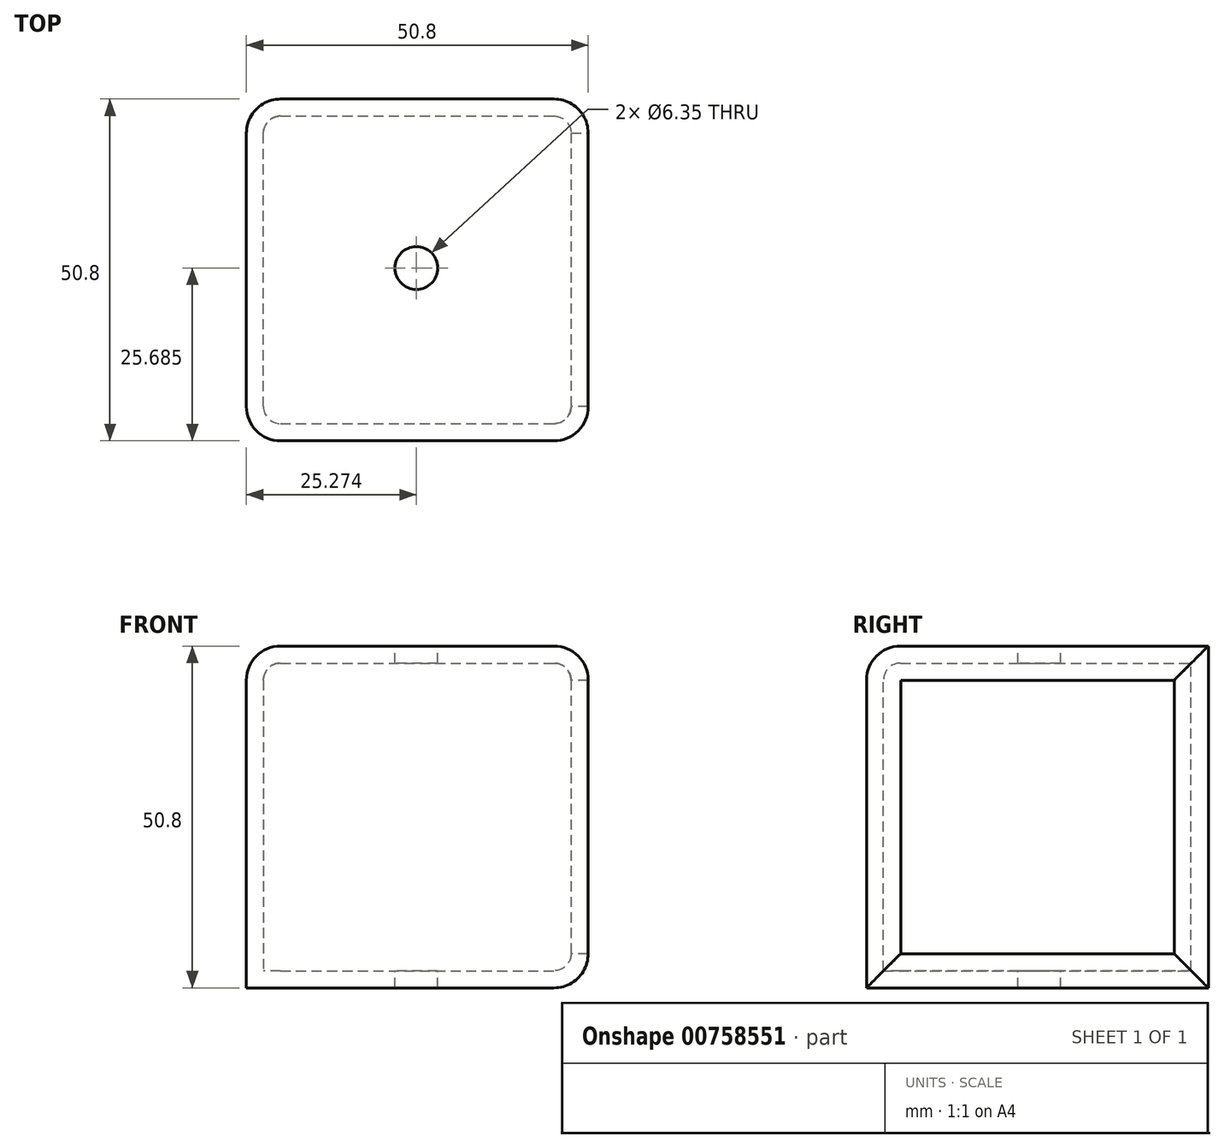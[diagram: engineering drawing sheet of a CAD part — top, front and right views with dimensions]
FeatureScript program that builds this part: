
annotation { "Feature Type Name" : "Feature", "Feature Type Description" : "" }
export const myFeature = defineFeature(function(context is Context, id is Id, definition is map)
    precondition{}
    {
        {
            var Q0;
            Q0=qCreatedBy(makeId("Top.planeOp"),FACE);
            var sketch = newSketch(context, id + "F0", { "sketchPlane" : qUnion([Q0])});
            skLineSegment(sketch, "E0", {"start": v(-54.42, -6.82) * mm, "end": v(-3.62, -6.82) * mm});
            skLineSegment(sketch, "E1", {"start": v(-3.62, -6.82) * mm, "end": v(-54.42, -6.82) * mm});
            skLineSegment(sketch, "E2", {"start": v(-54.42, -6.82) * mm, "end": v(-54.42, -57.62) * mm});
            skLineSegment(sketch, "E3", {"start": v(-54.42, -57.62) * mm, "end": v(-3.62, -57.62) * mm});
            skLineSegment(sketch, "E4", {"start": v(-3.62, -6.82) * mm, "end": v(-3.62, -57.62) * mm});
            skSolve(sketch);
        }
        {
            var Q0;
            Q0=qSketchRegion(id+"F0",true);
            extrude(context, id + "F1", {"entities" : qUnion([Q0]), "depth" : 50.8 * mm, "offsetDistance" : 25.4 * mm});
        }
        {
            var Q0;
            Q0=makeQuery(id+"F1.opExtrude","SWEPT_FACE",FACE,{"disambiguationData":[OSD([sQuery(id+"F0.wireOp",EDGE,"E3")])]});
            var sketch = newSketch(context, id + "F2", { "sketchPlane" : qUnion([Q0])});
            skSolve(sketch);
        }
        {
            var Q0;
            Q0=makeQuery(id+"F1.opExtrude","CAP_EDGE",EDGE,{"disambiguationData":[OSD([sQuery(id+"F0.wireOp",EDGE,"E3")])],"isStart":false});
            var Q1;
            Q1=makeQuery(id+"F1.opExtrude","CAP_EDGE",EDGE,{"disambiguationData":[OSD([sQuery(id+"F0.wireOp",EDGE,"E2")])],"isStart":false});
            var Q2;
            Q2=makeQuery(id+"F1.opExtrude","CAP_EDGE",EDGE,{"disambiguationData":[OSD([sQuery(id+"F0.wireOp",EDGE,"E1")])],"isStart":false});
            var Q3;
            Q3=makeQuery(id+"F1.opExtrude","CAP_EDGE",EDGE,{"disambiguationData":[OSD([sQuery(id+"F0.wireOp",EDGE,"E4")])],"isStart":false});
            var Q4;
            Q4=makeQuery(id+"F1.opExtrude","SWEPT_EDGE",EDGE,{"disambiguationData":[OSD([sQuery(id+"F0.wireOp",EDGE,"E2"),sQuery(id+"F0.wireOp",EDGE,"E3")])]});
            var Q5;
            Q5=makeQuery(id+"F1.opExtrude","SWEPT_EDGE",EDGE,{"disambiguationData":[OSD([sQuery(id+"F0.wireOp",EDGE,"E1"),sQuery(id+"F0.wireOp",EDGE,"E2")])]});
            var Q6;
            Q6=makeQuery(id+"F1.opExtrude","SWEPT_EDGE",EDGE,{"disambiguationData":[OSD([sQuery(id+"F0.wireOp",EDGE,"E1"),sQuery(id+"F0.wireOp",EDGE,"E4")])]});
            var Q7;
            Q7=makeQuery(id+"F1.opExtrude","SWEPT_FACE",FACE,{"disambiguationData":[OSD([sQuery(id+"F0.wireOp",EDGE,"E4")])]});
            fillet(context, id + "F3", {"entities" : qUnion([Q0, Q1, Q2, Q3, Q4, Q5, Q6, Q7]), "radius" : 5.08 * mm, "tangentPropagation" : true, "allowEdgeOverflow" : false});
        }
        {
            var Q0;
            Q0=makeQuery(id+"F1.opExtrude","CAP_FACE",FACE,{"disambiguationData":[OSD([sQuery(id+"F0.wireOp",EDGE,"E1"),sQuery(id+"F0.wireOp",EDGE,"E2"),sQuery(id+"F0.wireOp",EDGE,"E3"),sQuery(id+"F0.wireOp",EDGE,"E4")])],"isStart":false});
            var sketch = newSketch(context, id + "F4", { "sketchPlane" : qUnion([Q0])});
            skLineSegment(sketch, "E5", {"start": v(-49.34, -11.9) * mm, "end": v(-8.7, -52.54) * mm});
            skLineSegment(sketch, "E6", {"start": v(-49.34, -52.54) * mm, "end": v(-8.7, -11.9) * mm});
            skSolve(sketch);
        }
        {
            var Q0;
            Q0=makeQuery(id+"F1.opExtrude","SWEPT_FACE",FACE,{"disambiguationData":[OSD([sQuery(id+"F0.wireOp",EDGE,"E4")])]});
            shell(context, id + "F5", {"entities" : qUnion([Q0]), "thickness" : 2.54 * mm});
        }
        {
            var Q0;
            {var subQ1=sQuery(id+"F0.wireOp",EDGE,"E3");var subQ2=sQuery(id+"F0.wireOp",EDGE,"E2");var subQ3=sQuery(id+"F0.wireOp",EDGE,"E1");var subQ4=makeQuery(id+"F1.opExtrude","CAP_FACE",FACE,{"disambiguationData":[OSD([subQ3,subQ2,subQ1,sQuery(id+"F0.wireOp",EDGE,"E4")])],"isStart":false});var subQ5=makeQuery(id+"F3.opFillet","BLEND_EDGE",EDGE,{"blendedFrom":[makeQuery(id+"F1.opExtrude","CAP_EDGE",EDGE,{"disambiguationData":[OSD([subQ2])],"isStart":false}),subQ4],"blendedInto":[subQ4]});Q0=makeQuery(id+"F4.imprint","IMPRINT",FACE,{"disambiguationData":[TD([[makeQuery(id+"F4.imprint","IMPRINT",EDGE,{"derivedFrom":subQ5}),1.0]])]});}
            var sketch = newSketch(context, id + "F6", { "sketchPlane" : qUnion([Q0])});
            skPoint(sketch, "E7", {"position": v(-29.15, -31.94) * mm});
            skPoint(sketch, "E8", {"position": v(-29.02, -32.22) * mm});
            skSolve(sketch);
        }
        {
            var Q0;
            Q0=sQuery(id+"F6.wireOp",VERTEX,"E7");
            var Q1;
            Q1=makeQuery(id+"F1.opExtrude","SWEPT_BODY",BODY,{"disambiguationData":[OSD([sQuery(id+"F0.wireOp",EDGE,"E1"),sQuery(id+"F0.wireOp",EDGE,"E2"),sQuery(id+"F0.wireOp",EDGE,"E3"),sQuery(id+"F0.wireOp",EDGE,"E4")])]});
            hole(context, id + "F7", {"style" : HoleStyle.SIMPLE, "endStyle" : HoleEndStyle.THROUGH, "holeDiameter" : 6.35 * mm, "majorDiameter" : 5 * mm, "isTappedThrough" : true, "tappedDepth" : 12.7 * mm, "tapClearance" : 3, "locations" : qUnion([Q0]), "scope" : qUnion([Q1])});
        }
    });
